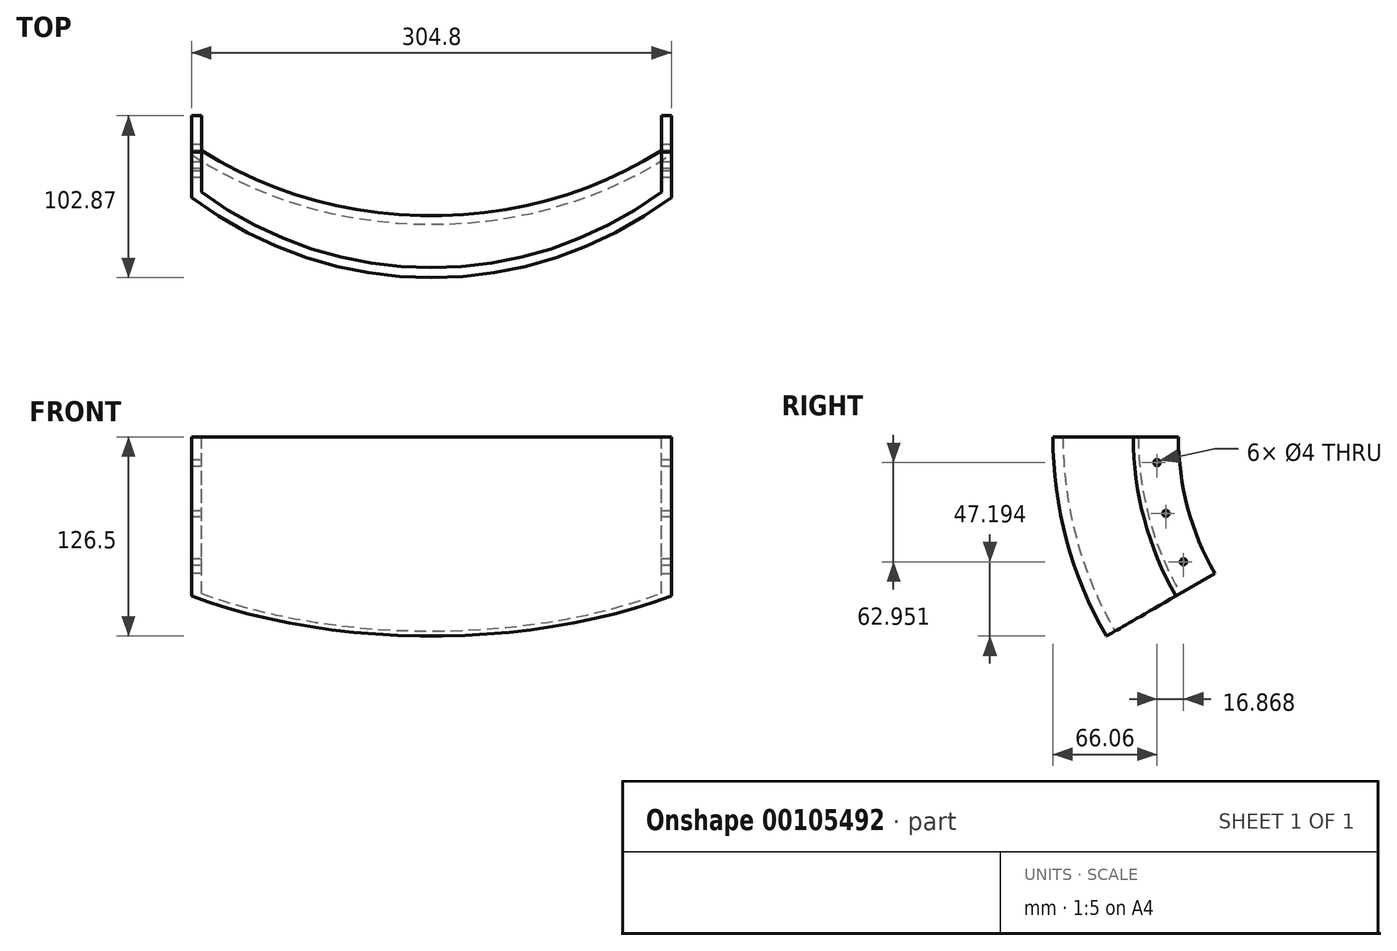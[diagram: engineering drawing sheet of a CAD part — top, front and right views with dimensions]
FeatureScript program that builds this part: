
annotation { "Feature Type Name" : "Feature", "Feature Type Description" : "" }
export const myFeature = defineFeature(function(context is Context, id is Id, definition is map)
    precondition{}
    {
        {
            var Q0;
            Q0=qCreatedBy(makeId("Top.planeOp"),FACE);
            var sketch = newSketch(context, id + "F0", { "sketchPlane" : qUnion([Q0])});
            skArc(sketch, "E0", {"start": v(-152.4, -201.95) * mm, "mid": v(0, -253) * mm, "end": v(152.4, -201.95) * mm});
            skArc(sketch, "E1.0", {"start": v(-146.05, -198.76) * mm, "mid": v(0, -246.65) * mm, "end": v(146.05, -198.76) * mm});
            skLineSegment(sketch, "E2", {"start": v(152.4, -201.95) * mm, "end": v(152.4, -173.36) * mm});
            skLineSegment(sketch, "E3.0", {"start": v(146.05, -198.76) * mm, "end": v(146.05, -173.36) * mm});
            skLineSegment(sketch, "E4", {"start": v(146.05, -173.36) * mm, "end": v(152.4, -173.36) * mm});
            skLineSegment(sketch, "E5", {"start": v(0, 0) * mm, "end": v(0, -204.73) * mm, "construction": true});
            skLineSegment(sketch, "E6.MirrorCS", {"start": v(-146.05, -198.76) * mm, "end": v(-146.05, -173.36) * mm});
            skLineSegment(sketch, "E7.MirrorCS", {"start": v(-152.4, -201.95) * mm, "end": v(-152.4, -173.36) * mm});
            skLineSegment(sketch, "E8.MirrorCS", {"start": v(-146.05, -173.36) * mm, "end": v(-152.4, -173.36) * mm});
            skLineSegment(sketch, "E9", {"start": v(0, 0) * mm, "end": v(153.5, 0) * mm, "construction": true});
            skSolve(sketch);
        }
        {
            var Q0;
            Q0=qSketchRegion(id+"F0",true);
            var Q1;
            Q1=sQuery(id+"F0.wireOp",EDGE,"E9");
            revolve(context, id + "F1", {"entities" : qUnion([Q0]), "axis" : qUnion([Q1]), "revolveType" : RevolveType.ONE_DIRECTION, "angle" : 30 * degree});
        }
        {
            var Q0;
            Q0=makeQuery(id+"F1.opRevolve","SWEPT_FACE",FACE,{"disambiguationData":[OSD([sQuery(id+"F0.wireOp",EDGE,"E2")])]});
            var sketch = newSketch(context, id + "F2", { "sketchPlane" : qUnion([Q0])});
            skCircle(sketch, "E10", {"center": v(-16.36, 186.94) * mm, "radius": 2 * mm});
            skCircle(sketch, "E11.1.0", {"center": v(-48.57, 181.26) * mm, "radius": 2 * mm});
            skCircle(sketch, "E11.2.0", {"center": v(-79.3, 170.07) * mm, "radius": 2 * mm});
            skCircle(sketch, "E11.3.0", {"center": v(-107.63, 153.72) * mm, "radius": 2 * mm});
            skCircle(sketch, "E11.4.0", {"center": v(-132.7, 132.7) * mm, "radius": 2 * mm});
            skCircle(sketch, "E11.5.0", {"center": v(-153.72, 107.63) * mm, "radius": 2 * mm});
            skCircle(sketch, "E11.6.0", {"center": v(-170.07, 79.3) * mm, "radius": 2 * mm});
            skCircle(sketch, "E11.7.0", {"center": v(-181.26, 48.57) * mm, "radius": 2 * mm});
            skCircle(sketch, "E11.8.0", {"center": v(-186.94, 16.36) * mm, "radius": 2 * mm});
            skCircle(sketch, "E11.9.0", {"center": v(-186.94, -16.36) * mm, "radius": 2 * mm});
            skCircle(sketch, "E11.10.0", {"center": v(-181.26, -48.57) * mm, "radius": 2 * mm});
            skCircle(sketch, "E11.11.0", {"center": v(-170.07, -79.3) * mm, "radius": 2 * mm});
            skCircle(sketch, "E11.12.0", {"center": v(-153.72, -107.63) * mm, "radius": 2 * mm});
            skCircle(sketch, "E11.13.0", {"center": v(-132.7, -132.7) * mm, "radius": 2 * mm});
            skCircle(sketch, "E11.14.0", {"center": v(-107.63, -153.72) * mm, "radius": 2 * mm});
            skCircle(sketch, "E11.15.0", {"center": v(-79.3, -170.07) * mm, "radius": 2 * mm});
            skCircle(sketch, "E11.16.0", {"center": v(-48.57, -181.26) * mm, "radius": 2 * mm});
            skCircle(sketch, "E11.17.0", {"center": v(-16.36, -186.94) * mm, "radius": 2 * mm});
            skCircle(sketch, "E11.18.0", {"center": v(16.36, -186.94) * mm, "radius": 2 * mm});
            skCircle(sketch, "E11.19.0", {"center": v(48.57, -181.26) * mm, "radius": 2 * mm});
            skCircle(sketch, "E11.20.0", {"center": v(79.3, -170.07) * mm, "radius": 2 * mm});
            skCircle(sketch, "E11.21.0", {"center": v(107.63, -153.72) * mm, "radius": 2 * mm});
            skCircle(sketch, "E11.22.0", {"center": v(132.7, -132.7) * mm, "radius": 2 * mm});
            skCircle(sketch, "E11.23.0", {"center": v(153.72, -107.63) * mm, "radius": 2 * mm});
            skCircle(sketch, "E11.24.0", {"center": v(170.07, -79.3) * mm, "radius": 2 * mm});
            skCircle(sketch, "E11.25.0", {"center": v(181.26, -48.57) * mm, "radius": 2 * mm});
            skCircle(sketch, "E11.26.0", {"center": v(186.94, -16.36) * mm, "radius": 2 * mm});
            skCircle(sketch, "E11.27.0", {"center": v(186.94, 16.36) * mm, "radius": 2 * mm});
            skCircle(sketch, "E11.28.0", {"center": v(181.26, 48.57) * mm, "radius": 2 * mm});
            skCircle(sketch, "E11.29.0", {"center": v(170.07, 79.3) * mm, "radius": 2 * mm});
            skCircle(sketch, "E11.30.0", {"center": v(153.72, 107.63) * mm, "radius": 2 * mm});
            skCircle(sketch, "E11.31.0", {"center": v(132.7, 132.7) * mm, "radius": 2 * mm});
            skCircle(sketch, "E11.32.0", {"center": v(107.63, 153.72) * mm, "radius": 2 * mm});
            skCircle(sketch, "E11.33.0", {"center": v(79.3, 170.07) * mm, "radius": 2 * mm});
            skCircle(sketch, "E11.34.0", {"center": v(48.57, 181.26) * mm, "radius": 2 * mm});
            skCircle(sketch, "E11.35.0", {"center": v(16.36, 186.94) * mm, "radius": 2 * mm});
            skPoint(sketch, "E11.center", {"position": v(0, 0) * mm});
            skSolve(sketch);
        }
        {
            var Q0;
            Q0=qSketchRegion(id+"F2",true);
            extrude(context, id + "F3", {"entities" : qUnion([Q0]), "operationType" : NewBodyOperationType.REMOVE, "endBound" : BoundingType.THROUGH_ALL, "oppositeDirection" : true, "depth" : 25.4 * mm});
        }
    });
